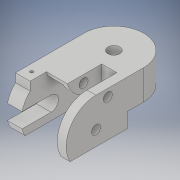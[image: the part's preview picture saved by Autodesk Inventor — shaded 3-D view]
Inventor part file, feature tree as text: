
AUTODESK INVENTOR PART (.ipt)
format: ipt  version: 2018 (Build 220112000, 112)  size: 256,512 bytes
history: native  units: in
note: dims shown in document units (in); Inventor stores cm internally (conversion verified against a paired STEP export)
features: sketch x18, extrude x17
ambient origin geometry x8: Origin, YZ Plane, XZ Plane, XY Plane, X Axis, Y Axis, Z Axis, Center Point
bodies: Solid1 (feature_tree)
feature tree (35):
  sketch  "Sketch1"  dims[d1=0.1181in d5=0.7874in d6=0.0in]
  extrude  "Extrusion1"  Depth=0.7874in TaperAngle=0.0deg
  extrude  "Extrusion2"  Depth=0.1929in
  extrude  "Extrusion3"  Depth=0.4764in
  extrude  "Extrusion4"  Depth=0.1969in
  extrude  "Extrusion5"  Depth=0.1969in
  extrude  "Extrusion6"  Depth=0.1575in
  extrude  "Extrusion7"  Depth=0.3543in
  extrude  "Extrusion8"  Depth=0.1575in TaperAngle=0.0deg
  extrude  "Extrusion9"  Depth=0.4331in
  extrude  "Extrusion10"  Depth=0.1181in
  extrude  "Extrusion11"  Depth=0.1181in
  extrude  "Extrusion12"  Depth=0.0591in
  extrude  "Extrusion13"  Depth=0.0591in
  extrude  "Extrusion14"  Depth=0.2756in
  extrude  "Extrusion15"  Depth=0.1929in TaperAngle=0.0deg
  extrude  "Extrusion16"  Depth=0.1929in TaperAngle=0.0deg
  extrude  "Extrusion17"  Depth=0.1909in
  sketch  "Sketch2"  dims[d7=0.7874in d8=0.0in d10=0.1929in]
  sketch  "Sketch3"  dims[d11=0.7874in d12=0.4764in]
  sketch  "Sketch5"  dims[d13=0.7874in d14=0.0in d15=0.1969in]
  sketch  "Sketch6"  dims[d16=0.1969in d17=0.0in d18=0.1969in]
  sketch  "Sketch7"  dims[d19=0.7874in d20=0.0in d21=0.1575in]
  sketch  "Sketch8"  dims[d22=0.7874in d23=0.0in d24=0.3543in]
  sketch  "Sketch9"  dims[d25=0.3937in d26=0.0in d31=0.1575in d32=0.0in]
  sketch  "Sketch12"  dims[d33=0.4331in d34=0.4331in]
  sketch  "Sketch13"  dims[d35=0.1969in d36=0.0in d39=0.1181in]
  sketch  "Sketch14"  dims[d40=0.1969in d41=0.0in d43=0.1181in]
  sketch  "Sketch15"  dims[d44=0.1969in d45=0.0in d46=0.0591in]
  sketch  "Sketch16"  dims[d47=0.0591in d48=0.5118in]
  sketch  "Sketch17"  dims[d49=0.2756in d50=0.0in d51=0.2756in]
  sketch  "Sketch18"  dims[d52=0.2953in d53=0.1929in d54=0.0in]
  sketch  "Sketch19"  dims[d55=0.0394in d56=0.1929in d57=0.0in]
  sketch  "Sketch20"  dims[d58=0.1181in d59=0.1909in]
  sketch  "Sketch21"  dims[d60=0.0787in d61=0.4724in d62=0.0in d63=0.0787in d64=0.0in d65=0.2756in d66=0.0in]
